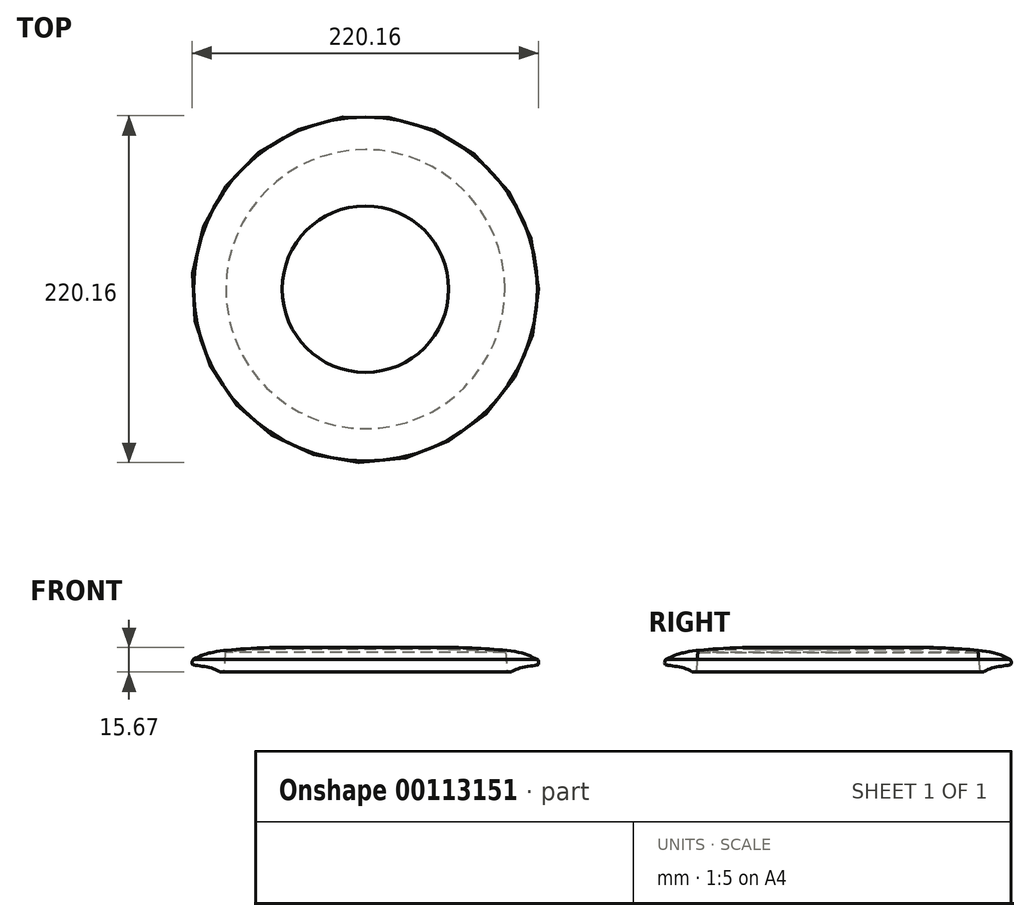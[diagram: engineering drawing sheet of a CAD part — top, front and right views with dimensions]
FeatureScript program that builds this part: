
annotation { "Feature Type Name" : "Feature", "Feature Type Description" : "" }
export const myFeature = defineFeature(function(context is Context, id is Id, definition is map)
    precondition{}
    {
        {
            var Q0;
            Q0=qCreatedBy(makeId("Front.planeOp"),FACE);
            var sketch = newSketch(context, id + "F0", { "sketchPlane" : qUnion([Q0])});
            skLineSegment(sketch, "E0", {"start": v(0, -2.04) * mm, "end": v(0, -3.27) * mm});
            skLineSegment(sketch, "E1", {"start": v(0, -2.04) * mm, "end": v(52.87, -2.04) * mm});
            skLineSegment(sketch, "E2", {"start": v(0, -3.27) * mm, "end": v(52.87, -3.27) * mm});
            skFitSpline(sketch, "E3", {"points": [v(52.87, -3.27) * mm, v(84.54, -4.66) * mm, v(88.61, -5.13) * mm], "startDerivative": vector(63.68, -0.5) * mm, "endDerivative": vector(4.78, -2.1) * mm});
            skFitSpline(sketch, "E4", {"points": [v(52.87, -2.04) * mm, v(79.7, -3.1) * mm, v(100.08, -5.86) * mm, v(109.16, -9.75) * mm], "startDerivative": vector(73.65, -0.83) * mm, "endDerivative": vector(33.07, -17.45) * mm});
            skFitSpline(sketch, "E5", {"points": [v(88.61, -5.13) * mm, v(89.02, -5.45) * mm, v(90.03, -16.4) * mm, v(90.8, -17.61) * mm, v(92.27, -17.64) * mm, v(93.35, -17.1) * mm, v(100.13, -14.56) * mm, v(109.2, -13.16) * mm, v(110, -12.43) * mm, v(109.9, -10.6) * mm, v(109.16, -9.75) * mm], "startDerivative": vector(20.93, -8.5) * mm, "endDerivative": vector(-13.41, 10.54) * mm});
            skLineSegment(sketch, "E6", {"start": v(0, -2.04) * mm, "end": v(110, -2.04) * mm, "construction": true});
            skSolve(sketch);
        }
        {
            var Q0;
            Q0=makeQuery(id+"F0.imprint","IMPRINT",FACE,{"disambiguationData":[TD([[makeQuery(id+"F0.imprint","IMPRINT",EDGE,{"derivedFrom":sQuery(id+"F0.wireOp",EDGE,"E0")}),1.0]])]});
            var Q1;
            Q1=sQuery(id+"F0.wireOp",EDGE,"E0");
            revolve(context, id + "F1", {"entities" : qUnion([Q0]), "axis" : qUnion([Q1]), "revolveType" : RevolveType.FULL});
        }
    });
